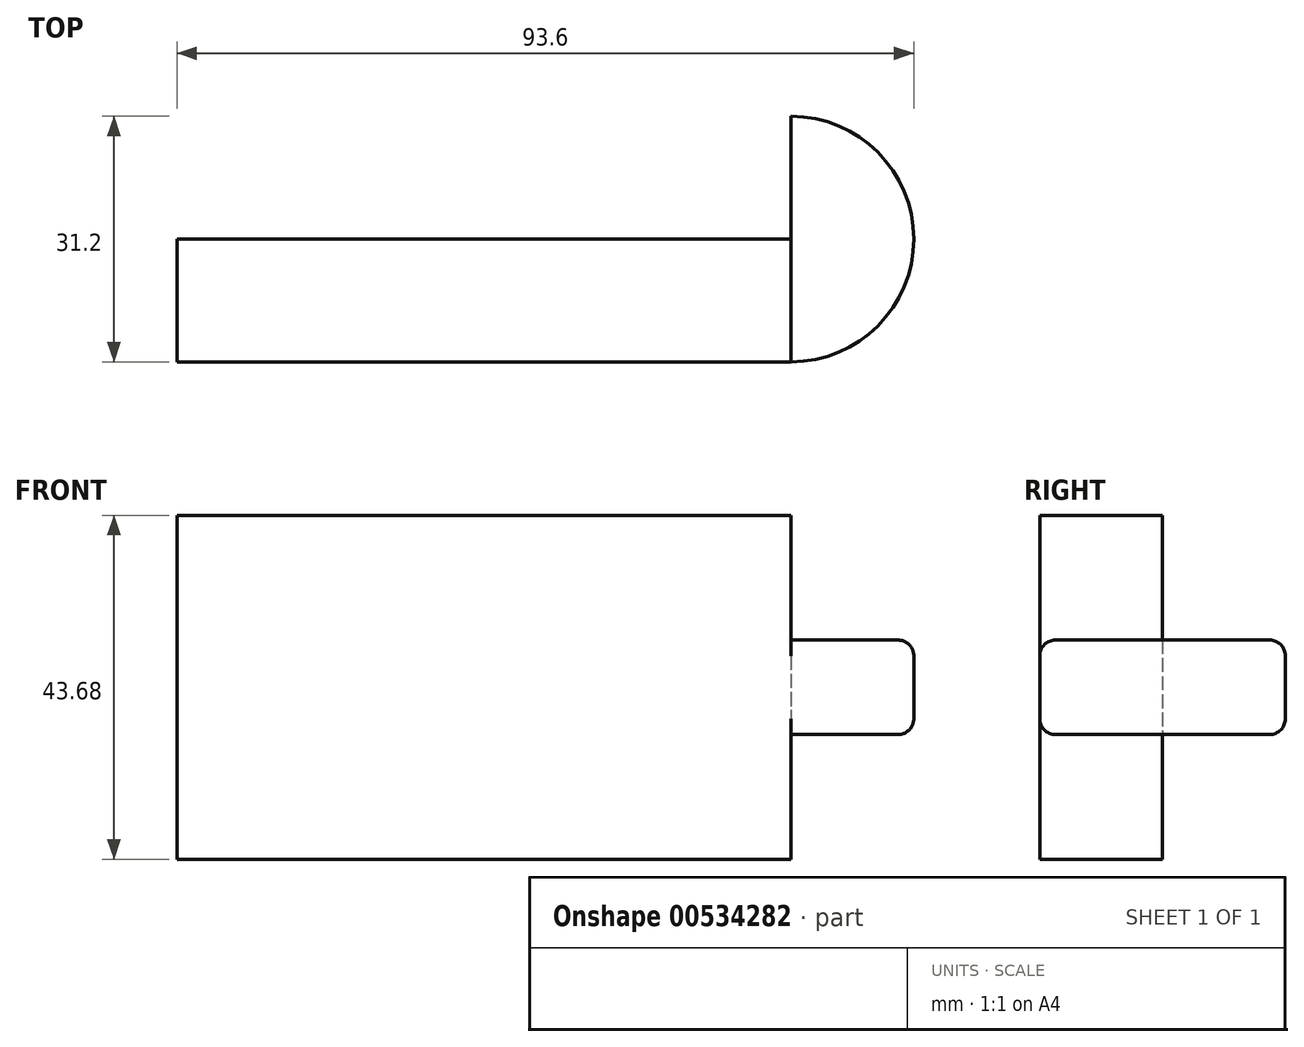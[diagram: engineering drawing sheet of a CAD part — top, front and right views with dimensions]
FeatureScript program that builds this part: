
annotation { "Feature Type Name" : "Feature", "Feature Type Description" : "" }
export const myFeature = defineFeature(function(context is Context, id is Id, definition is map)
    precondition{}
    {
        {
            var Q0;
            Q0=qCreatedBy(makeId("Front.planeOp"),FACE);
            var sketch = newSketch(context, id + "F0", { "sketchPlane" : qUnion([Q0])});
            skLineSegment(sketch, "E0.bottom", {"start": v(39, 21.84) * mm, "end": v(-39, 21.84) * mm});
            skLineSegment(sketch, "E0.top", {"start": v(39, -21.84) * mm, "end": v(-39, -21.84) * mm});
            skLineSegment(sketch, "E0.left", {"start": v(39, 21.84) * mm, "end": v(39, -21.84) * mm});
            skLineSegment(sketch, "E0.right", {"start": v(-39, 21.84) * mm, "end": v(-39, -21.84) * mm});
            skPoint(sketch, "E0.middle", {"position": v(0, 0) * mm});
            skSolve(sketch);
        }
        {
            var Q0;
            Q0=makeQuery(id+"F0.imprint","IMPRINT",FACE,{"disambiguationData":[TD([[makeQuery(id+"F0.imprint","IMPRINT",EDGE,{"derivedFrom":sQuery(id+"F0.wireOp",EDGE,"E0.bottom")}),1.0]])]});
            extrude(context, id + "F1", {"entities" : qUnion([Q0]), "endBound" : BoundingType.SYMMETRIC, "depth" : 15.6 * mm, "offsetDistance" : 25 * mm});
        }
        {
            var Q0;
            Q0=qCreatedBy(makeId("Top.planeOp"),FACE);
            var sketch = newSketch(context, id + "F2", { "sketchPlane" : qUnion([Q0])});
            skArc(sketch, "E1", {"start": v(39, -7.8) * mm, "mid": v(54.6, 7.8) * mm, "end": v(39, 23.4) * mm});
            skLineSegment(sketch, "E2", {"start": v(39, 7.8) * mm, "end": v(39, 23.4) * mm});
            skLineSegment(sketch, "E3", {"start": v(39, 7.8) * mm, "end": v(39, -7.8) * mm});
            skSolve(sketch);
        }
        {
            var Q0;
            Q0=makeQuery(id+"F2.imprint","IMPRINT",FACE,{"disambiguationData":[TD([[makeQuery(id+"F2.imprint","IMPRINT",EDGE,{"derivedFrom":sQuery(id+"F2.wireOp",EDGE,"E1")}),1.0]])]});
            extrude(context, id + "F3", {"entities" : qUnion([Q0]), "operationType" : NewBodyOperationType.ADD, "endBound" : BoundingType.SYMMETRIC, "depth" : 12 * mm, "offsetDistance" : 25 * mm});
        }
        {
            var Q0;
            Q0=makeQuery(id+"F3.opExtrude","CAP_EDGE",EDGE,{"disambiguationData":[OSD([sQuery(id+"F2.wireOp",EDGE,"E1")])],"isStart":false});
            var Q1;
            Q1=makeQuery(id+"F3.opExtrude","CAP_EDGE",EDGE,{"disambiguationData":[OSD([sQuery(id+"F2.wireOp",EDGE,"E1")])],"isStart":true});
            fillet(context, id + "F4", {"entities" : qUnion([Q0, Q1]), "radius" : 2 * mm, "tangentPropagation" : true, "allowEdgeOverflow" : false});
        }
    });
